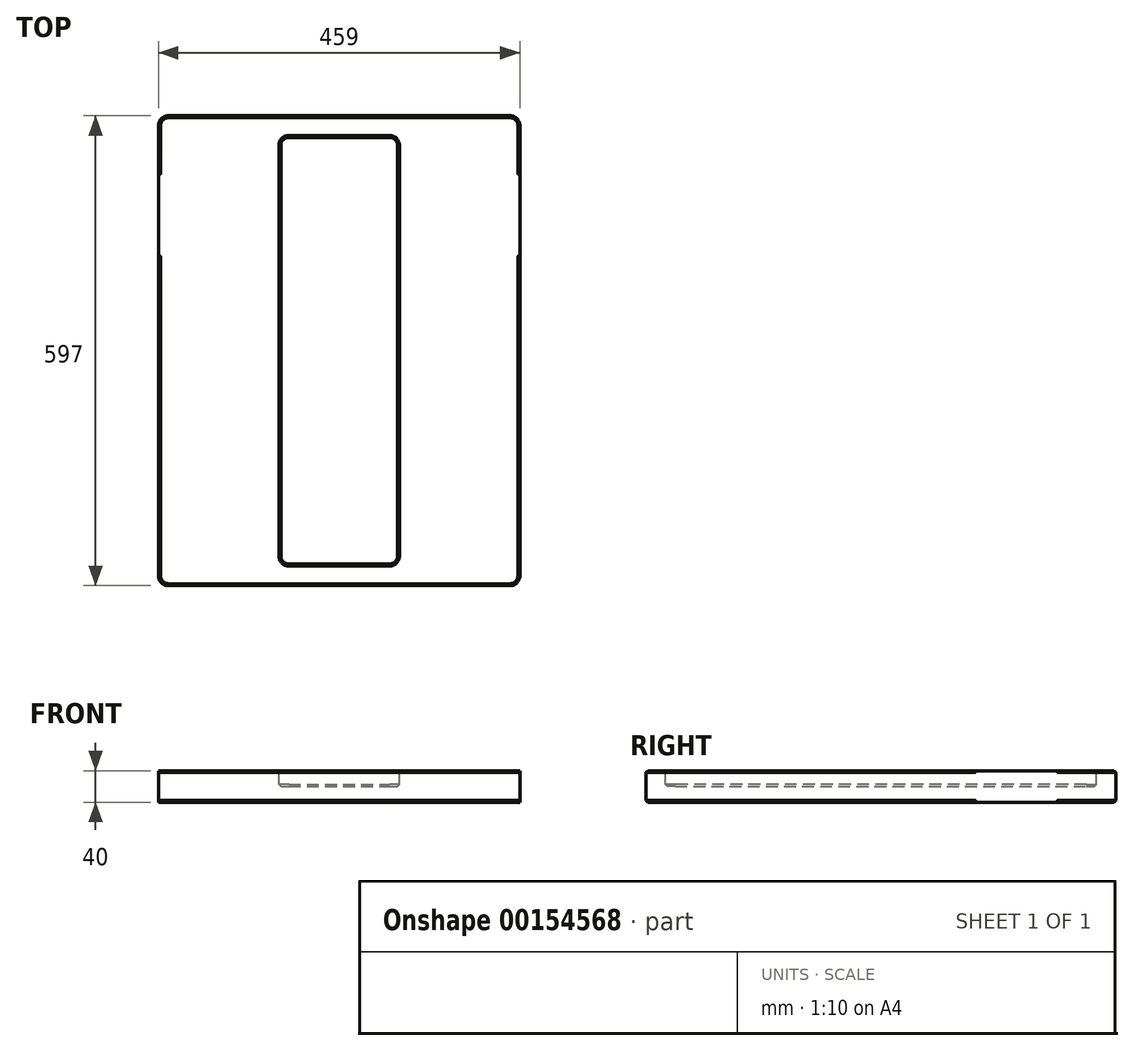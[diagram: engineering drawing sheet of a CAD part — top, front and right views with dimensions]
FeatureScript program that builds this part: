
annotation { "Feature Type Name" : "Feature", "Feature Type Description" : "" }
export const myFeature = defineFeature(function(context is Context, id is Id, definition is map)
    precondition{}
    {
        {
            var Q0;
            Q0=qCreatedBy(makeId("Top.planeOp"),FACE);
            var sketch = newSketch(context, id + "F0", { "sketchPlane" : qUnion([Q0])});
            skLineSegment(sketch, "E0.bottom", {"start": v(-12.5, 0) * mm, "end": v(-446.5, 0) * mm});
            skLineSegment(sketch, "E0.top", {"start": v(-12.5, 597) * mm, "end": v(-446.5, 597) * mm});
            skLineSegment(sketch, "E0.left", {"start": v(0, 12.5) * mm, "end": v(0, 584.5) * mm});
            skLineSegment(sketch, "E0.right", {"start": v(-459, 12.5) * mm, "end": v(-459, 584.5) * mm});
            skPoint(sketch, "E1.visualSharp", {"position": v(-459, 597) * mm});
            skArc(sketch, "E1.filletArc", {"start": v(-446.5, 597) * mm, "mid": v(-455.34, 593.34) * mm, "end": v(-459, 584.5) * mm});
            skPoint(sketch, "E2.visualSharp", {"position": v(0, 597) * mm});
            skArc(sketch, "E2.filletArc", {"start": v(0, 584.5) * mm, "mid": v(-3.66, 593.34) * mm, "end": v(-12.5, 597) * mm});
            skPoint(sketch, "E3.visualSharp", {"position": v(0, 0) * mm});
            skArc(sketch, "E3.filletArc", {"start": v(-12.5, 0) * mm, "mid": v(-3.66, 3.66) * mm, "end": v(0, 12.5) * mm});
            skPoint(sketch, "E4.visualSharp", {"position": v(-459, 0) * mm});
            skArc(sketch, "E4.filletArc", {"start": v(-459, 12.5) * mm, "mid": v(-455.34, 3.66) * mm, "end": v(-446.5, 0) * mm});
            skSolve(sketch);
        }
        {
            var Q0;
            Q0 = qSketchRegion(id + "F0", true);
            extrude(context, id + "F1", {"entities" : qUnion([Q0]), "depth" : 40 * mm});
        }
        {
            var Q0;
            Q0=makeQuery(id+"F1.opExtrude","CAP_FACE",FACE,{"disambiguationData":[OSD([sQuery(id+"F0.wireOp",EDGE,"E0.bottom"),sQuery(id+"F0.wireOp",EDGE,"E0.top"),sQuery(id+"F0.wireOp",EDGE,"E0.left"),sQuery(id+"F0.wireOp",EDGE,"E0.right"),sQuery(id+"F0.wireOp",EDGE,"E1.filletArc"),sQuery(id+"F0.wireOp",EDGE,"E2.filletArc"),sQuery(id+"F0.wireOp",EDGE,"E3.filletArc"),sQuery(id+"F0.wireOp",EDGE,"E4.filletArc")])],"isStart":false});
            var Q1;
            Q1=makeQuery(id+"F1.opExtrude","CAP_FACE",FACE,{"disambiguationData":[OSD([sQuery(id+"F0.wireOp",EDGE,"E0.bottom"),sQuery(id+"F0.wireOp",EDGE,"E0.top"),sQuery(id+"F0.wireOp",EDGE,"E0.left"),sQuery(id+"F0.wireOp",EDGE,"E0.right"),sQuery(id+"F0.wireOp",EDGE,"E1.filletArc"),sQuery(id+"F0.wireOp",EDGE,"E2.filletArc"),sQuery(id+"F0.wireOp",EDGE,"E3.filletArc"),sQuery(id+"F0.wireOp",EDGE,"E4.filletArc")])],"isStart":true});
            chamfer(context, id + "F2", {"entities" : qUnion([Q0, Q1]), "width" : 2.5 * mm, "tangentPropagation" : true});
        }
        {
            var Q0;
            Q0=makeQuery(id+"F1.opExtrude","SWEPT_FACE",FACE,{"disambiguationData":[OSD([sQuery(id+"F0.wireOp",EDGE,"E0.right")])]});
            var sketch = newSketch(context, id + "F3", { "sketchPlane" : qUnion([Q0])});
            skLineSegment(sketch, "E5.bottom", {"start": v(-419.5, 37.5) * mm, "end": v(-522, 37.5) * mm});
            skLineSegment(sketch, "E5.top", {"start": v(-419.5, 2.5) * mm, "end": v(-522, 2.5) * mm});
            skLineSegment(sketch, "E5.left", {"start": v(-419.5, 37.5) * mm, "end": v(-419.5, 2.5) * mm});
            skLineSegment(sketch, "E5.right", {"start": v(-522, 37.5) * mm, "end": v(-522, 2.5) * mm});
            skLineSegment(sketch, "E6.0", {"start": v(-419.5, 40) * mm, "end": v(-522, 40) * mm});
            skLineSegment(sketch, "E7.0", {"start": v(-419.5, 0) * mm, "end": v(-522, 0) * mm});
            skLineSegment(sketch, "E8", {"start": v(-522, 40) * mm, "end": v(-522, 37.5) * mm});
            skLineSegment(sketch, "E9", {"start": v(-522, 2.5) * mm, "end": v(-522, 0) * mm});
            skLineSegment(sketch, "E10", {"start": v(-419.5, 2.5) * mm, "end": v(-419.5, 0) * mm});
            skLineSegment(sketch, "E11", {"start": v(-419.5, 40) * mm, "end": v(-419.5, 37.5) * mm});
            skSolve(sketch);
        }
        {
            var Q0;
            Q0 = qSketchRegion(id + "F3", true);
            extrude(context, id + "F4", {"entities" : qUnion([Q0]), "operationType" : NewBodyOperationType.ADD, "oppositeDirection" : true, "depth" : 459 * mm});
        }
        {
            var Q0;
            Q0=makeQuery(id+"F4.boolean.opBoolean","MERGE",FACE,{"derivedFrom":[makeQuery(id+"F1.opExtrude","CAP_FACE",FACE,{"disambiguationData":[OSD([sQuery(id+"F0.wireOp",EDGE,"E0.bottom"),sQuery(id+"F0.wireOp",EDGE,"E0.top"),sQuery(id+"F0.wireOp",EDGE,"E0.left"),sQuery(id+"F0.wireOp",EDGE,"E0.right"),sQuery(id+"F0.wireOp",EDGE,"E1.filletArc"),sQuery(id+"F0.wireOp",EDGE,"E2.filletArc"),sQuery(id+"F0.wireOp",EDGE,"E3.filletArc"),sQuery(id+"F0.wireOp",EDGE,"E4.filletArc")])],"isStart":false}),makeQuery(id+"F4.opExtrude","SWEPT_FACE",FACE,{"disambiguationData":[OSD([sQuery(id+"F3.wireOp",EDGE,"E6.0")])]})]});
            var sketch = newSketch(context, id + "F5", { "sketchPlane" : qUnion([Q0])});
            skLineSegment(sketch, "E12.bottom", {"start": v(-293.5, 572) * mm, "end": v(-165.5, 572) * mm});
            skLineSegment(sketch, "E12.top", {"start": v(-293.5, 25) * mm, "end": v(-165.5, 25) * mm});
            skLineSegment(sketch, "E12.left", {"start": v(-306, 559.5) * mm, "end": v(-306, 37.5) * mm});
            skLineSegment(sketch, "E12.right", {"start": v(-153, 559.5) * mm, "end": v(-153, 37.5) * mm});
            skPoint(sketch, "E13.visualSharp", {"position": v(-306, 572) * mm});
            skArc(sketch, "E13.filletArc", {"start": v(-293.5, 572) * mm, "mid": v(-302.34, 568.34) * mm, "end": v(-306, 559.5) * mm});
            skPoint(sketch, "E14.visualSharp", {"position": v(-153, 572) * mm});
            skArc(sketch, "E14.filletArc", {"start": v(-153, 559.5) * mm, "mid": v(-156.66, 568.34) * mm, "end": v(-165.5, 572) * mm});
            skPoint(sketch, "E15.visualSharp", {"position": v(-153, 25) * mm});
            skArc(sketch, "E15.filletArc", {"start": v(-165.5, 25) * mm, "mid": v(-156.66, 28.66) * mm, "end": v(-153, 37.5) * mm});
            skPoint(sketch, "E16.visualSharp", {"position": v(-306, 25) * mm});
            skArc(sketch, "E16.filletArc", {"start": v(-306, 37.5) * mm, "mid": v(-302.34, 28.66) * mm, "end": v(-293.5, 25) * mm});
            skSolve(sketch);
        }
        {
            var Q0;
            Q0 = qSketchRegion(id + "F5", true);
            extrude(context, id + "F6", {"entities" : qUnion([Q0]), "operationType" : NewBodyOperationType.REMOVE, "oppositeDirection" : true, "depth" : 20 * mm});
        }
        {
            var Q0;
            Q0=makeQuery(id+"F6.boolean.opBoolean","COPY",EDGE,{"derivedFrom":makeQuery(id+"F6.opExtrude","CAP_EDGE",EDGE,{"disambiguationData":[OSD([sQuery(id+"F5.wireOp",EDGE,"E12.left")])],"isStart":true})});
            var Q1;
            Q1=makeQuery(id+"F6.boolean.opBoolean","COPY",EDGE,{"derivedFrom":makeQuery(id+"F6.opExtrude","CAP_EDGE",EDGE,{"disambiguationData":[OSD([sQuery(id+"F5.wireOp",EDGE,"E12.bottom")])],"isStart":false})});
            chamfer(context, id + "F7", {"entities" : qUnion([Q0, Q1]), "width" : 2.5 * mm, "tangentPropagation" : true});
        }
        {
            var Q0;
            {var subQ0=sQuery(id+"F0.wireOp",EDGE,"E0.left");Q0=makeQuery(id+"F4.boolean.opBoolean","INTERSECT",EDGE,{"derivedFrom":[makeQuery(id+"F2.opChamfer","BLEND_FACE",FACE,{"disambiguationData":[OSD([subQ0]),TDD([makeQuery(id+"F1.opExtrude","CAP_EDGE",EDGE,{"disambiguationData":[OSD([subQ0])],"isStart":false})])]}),makeQuery(id+"F4.opExtrude","SWEPT_FACE",FACE,{"disambiguationData":[OSD([sQuery(id+"F3.wireOp",EDGE,"E5.left"),sQuery(id+"F3.wireOp",EDGE,"E10"),sQuery(id+"F3.wireOp",EDGE,"E11")])]})]});}
            var Q1;
            {var subQ0=sQuery(id+"F0.wireOp",EDGE,"E0.left");Q1=makeQuery(id+"F4.boolean.opBoolean","INTERSECT",EDGE,{"derivedFrom":[makeQuery(id+"F2.opChamfer","BLEND_FACE",FACE,{"disambiguationData":[OSD([subQ0]),TDD([makeQuery(id+"F1.opExtrude","CAP_EDGE",EDGE,{"disambiguationData":[OSD([subQ0])],"isStart":false})])]}),makeQuery(id+"F4.opExtrude","SWEPT_FACE",FACE,{"disambiguationData":[OSD([sQuery(id+"F3.wireOp",EDGE,"E5.right"),sQuery(id+"F3.wireOp",EDGE,"E8"),sQuery(id+"F3.wireOp",EDGE,"E9")])]})]});}
            var Q2;
            {var subQ0=sQuery(id+"F0.wireOp",EDGE,"E0.left");Q2=makeQuery(id+"F4.boolean.opBoolean","INTERSECT",EDGE,{"derivedFrom":[makeQuery(id+"F2.opChamfer","BLEND_FACE",FACE,{"disambiguationData":[OSD([subQ0]),TDD([makeQuery(id+"F1.opExtrude","CAP_EDGE",EDGE,{"disambiguationData":[OSD([subQ0])],"isStart":true})])]}),makeQuery(id+"F4.opExtrude","SWEPT_FACE",FACE,{"disambiguationData":[OSD([sQuery(id+"F3.wireOp",EDGE,"E5.left"),sQuery(id+"F3.wireOp",EDGE,"E10"),sQuery(id+"F3.wireOp",EDGE,"E11")])]})]});}
            var Q3;
            {var subQ0=sQuery(id+"F0.wireOp",EDGE,"E0.left");Q3=makeQuery(id+"F4.boolean.opBoolean","INTERSECT",EDGE,{"derivedFrom":[makeQuery(id+"F2.opChamfer","BLEND_FACE",FACE,{"disambiguationData":[OSD([subQ0]),TDD([makeQuery(id+"F1.opExtrude","CAP_EDGE",EDGE,{"disambiguationData":[OSD([subQ0])],"isStart":true})])]}),makeQuery(id+"F4.opExtrude","SWEPT_FACE",FACE,{"disambiguationData":[OSD([sQuery(id+"F3.wireOp",EDGE,"E5.right"),sQuery(id+"F3.wireOp",EDGE,"E8"),sQuery(id+"F3.wireOp",EDGE,"E9")])]})]});}
            var Q4;
            {var subQ0=sQuery(id+"F0.wireOp",EDGE,"E0.right");Q4=makeQuery(id+"F4.boolean.opBoolean","INTERSECT",EDGE,{"derivedFrom":[makeQuery(id+"F2.opChamfer","BLEND_FACE",FACE,{"disambiguationData":[OSD([subQ0]),TDD([makeQuery(id+"F1.opExtrude","CAP_EDGE",EDGE,{"disambiguationData":[OSD([subQ0])],"isStart":false})])]}),makeQuery(id+"F4.opExtrude","SWEPT_FACE",FACE,{"disambiguationData":[OSD([sQuery(id+"F3.wireOp",EDGE,"E5.right"),sQuery(id+"F3.wireOp",EDGE,"E8"),sQuery(id+"F3.wireOp",EDGE,"E9")])]})]});}
            var Q5;
            {var subQ0=sQuery(id+"F0.wireOp",EDGE,"E0.right");Q5=makeQuery(id+"F4.boolean.opBoolean","INTERSECT",EDGE,{"derivedFrom":[makeQuery(id+"F2.opChamfer","BLEND_FACE",FACE,{"disambiguationData":[OSD([subQ0]),TDD([makeQuery(id+"F1.opExtrude","CAP_EDGE",EDGE,{"disambiguationData":[OSD([subQ0])],"isStart":false})])]}),makeQuery(id+"F4.opExtrude","SWEPT_FACE",FACE,{"disambiguationData":[OSD([sQuery(id+"F3.wireOp",EDGE,"E5.left"),sQuery(id+"F3.wireOp",EDGE,"E10"),sQuery(id+"F3.wireOp",EDGE,"E11")])]})]});}
            var Q6;
            {var subQ0=sQuery(id+"F0.wireOp",EDGE,"E0.right");Q6=makeQuery(id+"F4.boolean.opBoolean","INTERSECT",EDGE,{"derivedFrom":[makeQuery(id+"F2.opChamfer","BLEND_FACE",FACE,{"disambiguationData":[OSD([subQ0]),TDD([makeQuery(id+"F1.opExtrude","CAP_EDGE",EDGE,{"disambiguationData":[OSD([subQ0])],"isStart":true})])]}),makeQuery(id+"F4.opExtrude","SWEPT_FACE",FACE,{"disambiguationData":[OSD([sQuery(id+"F3.wireOp",EDGE,"E5.right"),sQuery(id+"F3.wireOp",EDGE,"E8"),sQuery(id+"F3.wireOp",EDGE,"E9")])]})]});}
            var Q7;
            {var subQ0=sQuery(id+"F0.wireOp",EDGE,"E0.right");Q7=makeQuery(id+"F4.boolean.opBoolean","INTERSECT",EDGE,{"derivedFrom":[makeQuery(id+"F2.opChamfer","BLEND_FACE",FACE,{"disambiguationData":[OSD([subQ0]),TDD([makeQuery(id+"F1.opExtrude","CAP_EDGE",EDGE,{"disambiguationData":[OSD([subQ0])],"isStart":true})])]}),makeQuery(id+"F4.opExtrude","SWEPT_FACE",FACE,{"disambiguationData":[OSD([sQuery(id+"F3.wireOp",EDGE,"E5.left"),sQuery(id+"F3.wireOp",EDGE,"E10"),sQuery(id+"F3.wireOp",EDGE,"E11")])]})]});}
            fillet(context, id + "F8", {"entities" : qUnion([Q0, Q1, Q2, Q3, Q4, Q5, Q6, Q7]), "radius" : 1.75 * mm, "tangentPropagation" : true, "allowEdgeOverflow" : false});
        }
    });
